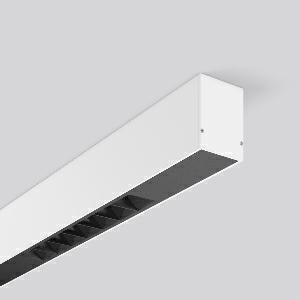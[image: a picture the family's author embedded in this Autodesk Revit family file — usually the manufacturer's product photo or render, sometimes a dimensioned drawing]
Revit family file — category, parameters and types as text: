
# Revit family: less_is_more_beamline_312495_002_1_76_6299
name_source: partatom
category: Lighting Fixtures
units: mm (PartAtom-declared; Revit-internal decimal feet)

## family parameters
Cut with Voids When Loaded = No
Host = Face
Light Source = No
Part Type = Normal
Room Calculation Point = No
Round Connector Dimension = Use Diameter
Shared = No

## types (1)
- LESS IS MORE BEAMLINE (1 x LED Modul 940, 1087.5 lm, 4000)
    Apparent Load = 47 VA
    CIE Flux Codes = 100 100 100 100 100
    Color Rendering = 92
    Color Temperature = 4000
    Default Elevation = 1800 mm
    Description = Series: LESS IS MORE BEAMLINE
Linear ceiling and wall luminaire for aesthetically sophisticated lighting. Luminaire with four LED light units. Housing: extruded aluminium profile, powder-coated. End cap aluminium powder-coated. LED light unit with MRS technology: Mini-Reflector-System made of metallised thermoplastic with prismatic black glare-suppressing frame for pleasant glare-free light (RUG < 10). Each LED light unit has 7 reflector elements. Narrow beam light distribution. LED unit with integrated converter interchangeable and removable. Suitable for through-wiring. 
Colour: traffic white, matt (RAL 9016)
Length: 2248 mm
Width: 57 mm
Height: 75 mm
Lamp: LED
Socket: without socket
Colour temperature: 4000K
Colour rendering index (CRI): 90
System power: 47 W
Rated luminous flux: 4350 lm
Luminous efficiency: 93 lm/W
Control gear: Converter, dimmable, DALI
Protection class: I
Type of protection: IP 20
    Height = 75 mm
    Lamp = 1 x LED Modul 940
    Lamp Light Flux = 1087.5 lm
    Lamp count = 1
    Length = 2248 mm
    Lifetime = 50000 h
    Luminous efficacy = 93 lm/W
    Manufacturer = RZB
    ModVariant = No
    Model = 312495.002.1.76
    Mounting Place = Ceiling, Wall
    Mounting Type = Surface mounted
    Number of Poles = 1
    OnlyDefault = Yes
    Power Factor = 1
    Product Name = LESS IS MORE BEAMLINE
    Product group = Surface mounted LED linear luminaires
    ProductGroupID = 307
    Protection Class = Protection class I
    Protection Degree = IP 20
    RLX_Detail_Level = 1
    RLX_Emergency_Light_Flux = 0 lm
    RLX_Emergency_Type = 0
    RLX_Emergency_Type_DB = No
    RlxData = <blob elided: 27589 chars, md5=bde8a108>
    Socket = socket
    Standby Power = 0 W
    System Light Flux = 4350 lm
    System Power = 47 W
    Type Comments = Product without accessories
    Type Image = 312483.002.jpg
    URL = http://relux.com
    VarID = ---
    Voltage = 230 V
    Voltage Range = 220-240 V
    Weight = 0.00 kg
    Width = 57 mm

## geometry (parser evidence)
native form markers: Blend x4, Sweep x21
no freeform markers — native parametric forms only
